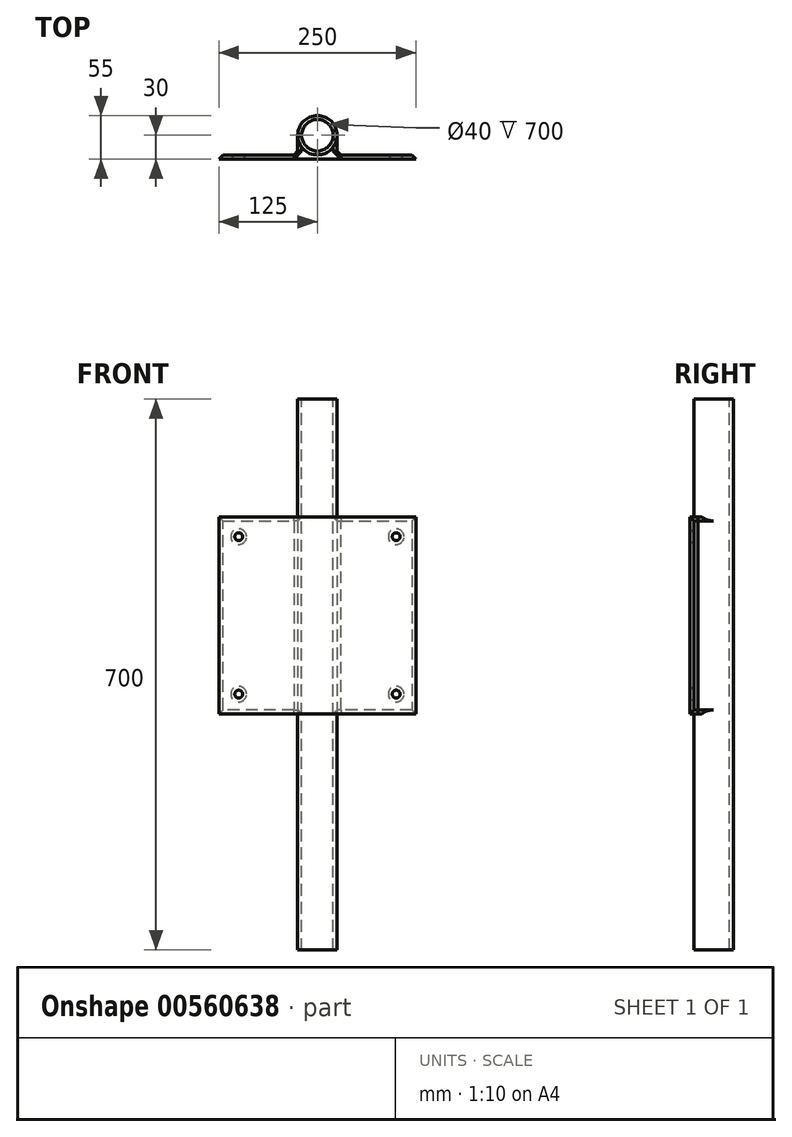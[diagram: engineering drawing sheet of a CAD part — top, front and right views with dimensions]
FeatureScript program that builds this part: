
annotation { "Feature Type Name" : "Feature", "Feature Type Description" : "" }
export const myFeature = defineFeature(function(context is Context, id is Id, definition is map)
    precondition{}
    {
        {
            var Q0;
            Q0=qCreatedBy(makeId("Top.planeOp"),FACE);
            var sketch = newSketch(context, id + "F0", { "sketchPlane" : qUnion([Q0])});
            skCircle(sketch, "E0", {"center": v(0, 0) * mm, "radius": 25 * mm});
            skLineSegment(sketch, "E1.bottom", {"start": v(-125, -25) * mm, "end": v(125, -25) * mm});
            skLineSegment(sketch, "E1.top", {"start": v(-125, -30) * mm, "end": v(125, -30) * mm});
            skLineSegment(sketch, "E1.left", {"start": v(-125, -25) * mm, "end": v(-125, -30) * mm});
            skLineSegment(sketch, "E1.right", {"start": v(125, -25) * mm, "end": v(125, -30) * mm});
            skLineSegment(sketch, "E2", {"start": v(25, 0) * mm, "end": v(25, -25) * mm});
            skLineSegment(sketch, "E3", {"start": v(-25, 0) * mm, "end": v(-25, -25) * mm});
            skSolve(sketch);
        }
        {
            var Q0;
            Q0 = qSketchRegion(id + "F0", true);
            var Q1;
            {var subQ0=sQuery(id+"F0.wireOp",EDGE,"E1.bottom");var subQ1=sQuery(id+"F0.wireOp",EDGE,"E0");var subQ2=makeQuery(id+"F0.imprint","INTERSECT",VERTEX,{"disambiguationData":[OD(0.0)],"derivedFrom":[subQ1,subQ0]});Q1=makeQuery(id+"F0.imprint","IMPRINT",FACE,{"disambiguationData":[TD([[makeQuery(id+"F0.imprint","IMPRINT",EDGE,{"disambiguationData":[TD([[subQ2,-1.0]])],"derivedFrom":subQ1}),1.0]])]});}
            extrude(context, id + "F1", {"entities" : qUnion([Q0, Q1]), "depth" : 250 * mm, "offsetDistance" : 25 * mm});
        }
        {
            var Q0;
            Q0=makeQuery(id+"F1.opExtrude","SWEPT_FACE",FACE,{"disambiguationData":[OSD([sQuery(id+"F0.wireOp",EDGE,"E1.top")])]});
            var sketch = newSketch(context, id + "F2", { "sketchPlane" : qUnion([Q0])});
            skLineSegment(sketch, "E4.bottom", {"start": v(-100, 225) * mm, "end": v(100, 225) * mm});
            skLineSegment(sketch, "E4.top", {"start": v(-100, 25) * mm, "end": v(100, 25) * mm});
            skLineSegment(sketch, "E4.left", {"start": v(-100, 225) * mm, "end": v(-100, 25) * mm});
            skLineSegment(sketch, "E4.right", {"start": v(100, 225) * mm, "end": v(100, 25) * mm});
            skCircle(sketch, "E5", {"center": v(-100, 225) * mm, "radius": 5 * mm});
            skCircle(sketch, "E6", {"center": v(100, 225) * mm, "radius": 5 * mm});
            skCircle(sketch, "E7", {"center": v(100, 25) * mm, "radius": 5 * mm});
            skCircle(sketch, "E8", {"center": v(-100, 25) * mm, "radius": 5 * mm});
            skSolve(sketch);
        }
        {
            var Q0;
            {var subQ0=sQuery(id+"F2.wireOp",EDGE,"E4.left");var subQ1=sQuery(id+"F2.wireOp",EDGE,"E4.bottom");var subQ2=makeQuery(id+"F2.imprint","INTERSECT",VERTEX,{"derivedFrom":[subQ1,subQ0]});Q0=makeQuery(id+"F2.imprint","IMPRINT",FACE,{"disambiguationData":[TD([[makeQuery(id+"F2.imprint","IMPRINT",EDGE,{"disambiguationData":[TD([[subQ2,-1.0]])],"derivedFrom":subQ1}),1.0]])]});}
            var Q1;
            {var subQ0=sQuery(id+"F2.wireOp",EDGE,"E4.left");var subQ1=sQuery(id+"F2.wireOp",EDGE,"E4.bottom");var subQ2=makeQuery(id+"F2.imprint","INTERSECT",VERTEX,{"derivedFrom":[subQ1,subQ0]});Q1=makeQuery(id+"F2.imprint","IMPRINT",FACE,{"disambiguationData":[TD([[makeQuery(id+"F2.imprint","IMPRINT",EDGE,{"disambiguationData":[TD([[subQ2,-1.0]])],"derivedFrom":subQ1}),-1.0]])]});}
            var Q2;
            {var subQ0=sQuery(id+"F2.wireOp",EDGE,"E4.right");var subQ1=sQuery(id+"F2.wireOp",EDGE,"E4.bottom");var subQ2=makeQuery(id+"F2.imprint","INTERSECT",VERTEX,{"derivedFrom":[subQ1,subQ0]});Q2=makeQuery(id+"F2.imprint","IMPRINT",FACE,{"disambiguationData":[TD([[makeQuery(id+"F2.imprint","IMPRINT",EDGE,{"disambiguationData":[TD([[subQ2,1.0]])],"derivedFrom":subQ1}),-1.0]])]});}
            var Q3;
            {var subQ0=sQuery(id+"F2.wireOp",EDGE,"E4.right");var subQ1=sQuery(id+"F2.wireOp",EDGE,"E4.bottom");var subQ2=makeQuery(id+"F2.imprint","INTERSECT",VERTEX,{"derivedFrom":[subQ1,subQ0]});Q3=makeQuery(id+"F2.imprint","IMPRINT",FACE,{"disambiguationData":[TD([[makeQuery(id+"F2.imprint","IMPRINT",EDGE,{"disambiguationData":[TD([[subQ2,1.0]])],"derivedFrom":subQ1}),1.0]])]});}
            var Q4;
            {var subQ0=sQuery(id+"F2.wireOp",EDGE,"E4.left");var subQ1=sQuery(id+"F2.wireOp",EDGE,"E4.top");var subQ2=makeQuery(id+"F2.imprint","INTERSECT",VERTEX,{"derivedFrom":[subQ1,subQ0]});Q4=makeQuery(id+"F2.imprint","IMPRINT",FACE,{"disambiguationData":[TD([[makeQuery(id+"F2.imprint","IMPRINT",EDGE,{"disambiguationData":[TD([[subQ2,-1.0]])],"derivedFrom":subQ1}),1.0]])]});}
            var Q5;
            {var subQ0=sQuery(id+"F2.wireOp",EDGE,"E4.left");var subQ1=sQuery(id+"F2.wireOp",EDGE,"E4.top");var subQ2=makeQuery(id+"F2.imprint","INTERSECT",VERTEX,{"derivedFrom":[subQ1,subQ0]});Q5=makeQuery(id+"F2.imprint","IMPRINT",FACE,{"disambiguationData":[TD([[makeQuery(id+"F2.imprint","IMPRINT",EDGE,{"disambiguationData":[TD([[subQ2,-1.0]])],"derivedFrom":subQ1}),-1.0]])]});}
            var Q6;
            {var subQ0=sQuery(id+"F2.wireOp",EDGE,"E4.right");var subQ1=sQuery(id+"F2.wireOp",EDGE,"E4.top");var subQ2=makeQuery(id+"F2.imprint","INTERSECT",VERTEX,{"derivedFrom":[subQ1,subQ0]});Q6=makeQuery(id+"F2.imprint","IMPRINT",FACE,{"disambiguationData":[TD([[makeQuery(id+"F2.imprint","IMPRINT",EDGE,{"disambiguationData":[TD([[subQ2,1.0]])],"derivedFrom":subQ1}),1.0]])]});}
            var Q7;
            {var subQ0=sQuery(id+"F2.wireOp",EDGE,"E4.right");var subQ1=sQuery(id+"F2.wireOp",EDGE,"E4.top");var subQ2=makeQuery(id+"F2.imprint","INTERSECT",VERTEX,{"derivedFrom":[subQ1,subQ0]});Q7=makeQuery(id+"F2.imprint","IMPRINT",FACE,{"disambiguationData":[TD([[makeQuery(id+"F2.imprint","IMPRINT",EDGE,{"disambiguationData":[TD([[subQ2,1.0]])],"derivedFrom":subQ1}),-1.0]])]});}
            extrude(context, id + "F3", {"entities" : qUnion([Q0, Q1, Q2, Q3, Q4, Q5, Q6, Q7]), "operationType" : NewBodyOperationType.REMOVE, "oppositeDirection" : true, "depth" : 25 * mm, "offsetDistance" : 25 * mm});
        }
        {
            var Q0;
            Q0=makeQuery(id+"F1.opExtrude","CAP_FACE",FACE,{"disambiguationData":[OSD([sQuery(id+"F0.wireOp",EDGE,"E0"),sQuery(id+"F0.wireOp",EDGE,"E1.bottom"),sQuery(id+"F0.wireOp",EDGE,"E1.top"),sQuery(id+"F0.wireOp",EDGE,"E1.left"),sQuery(id+"F0.wireOp",EDGE,"E1.right"),sQuery(id+"F0.wireOp",EDGE,"E2"),sQuery(id+"F0.wireOp",EDGE,"E3")])],"isStart":false});
            var sketch = newSketch(context, id + "F4", { "sketchPlane" : qUnion([Q0])});
            skCircle(sketch, "E9", {"center": v(0, 0) * mm, "radius": 25 * mm});
            skSolve(sketch);
        }
        {
            var Q0;
            Q0 = qSketchRegion(id + "F4", true);
            extrude(context, id + "F5", {"entities" : qUnion([Q0]), "operationType" : NewBodyOperationType.ADD, "depth" : 150 * mm, "offsetDistance" : 25 * mm});
        }
        {
            var Q0;
            Q0=makeQuery(id+"F1.opExtrude","CAP_FACE",FACE,{"disambiguationData":[OSD([sQuery(id+"F0.wireOp",EDGE,"E0"),sQuery(id+"F0.wireOp",EDGE,"E1.bottom"),sQuery(id+"F0.wireOp",EDGE,"E1.top"),sQuery(id+"F0.wireOp",EDGE,"E1.left"),sQuery(id+"F0.wireOp",EDGE,"E1.right"),sQuery(id+"F0.wireOp",EDGE,"E2"),sQuery(id+"F0.wireOp",EDGE,"E3")])],"isStart":true});
            var sketch = newSketch(context, id + "F6", { "sketchPlane" : qUnion([Q0])});
            skCircle(sketch, "E10", {"center": v(0, 0) * mm, "radius": 25 * mm});
            skSolve(sketch);
        }
        {
            var Q0;
            Q0 = qSketchRegion(id + "F6", true);
            extrude(context, id + "F7", {"entities" : qUnion([Q0]), "operationType" : NewBodyOperationType.ADD, "depth" : 300 * mm, "offsetDistance" : 25 * mm});
        }
        {
            var Q0;
            Q0=makeQuery(id+"F5.opExtrude","CAP_FACE",FACE,{"disambiguationData":[OSD([sQuery(id+"F4.wireOp",EDGE,"E9")])],"isStart":false});
            var sketch = newSketch(context, id + "F8", { "sketchPlane" : qUnion([Q0])});
            skCircle(sketch, "E11", {"center": v(0, 0) * mm, "radius": 20 * mm});
            skSolve(sketch);
        }
        {
            var Q0;
            Q0 = qSketchRegion(id + "F8", true);
            extrude(context, id + "F9", {"entities" : qUnion([Q0]), "operationType" : NewBodyOperationType.REMOVE, "endBound" : BoundingType.THROUGH_ALL, "oppositeDirection" : true, "depth" : 25 * mm, "offsetDistance" : 25 * mm});
        }
        {
            var Q0;
            {var subQ0=sQuery(id+"F0.wireOp",EDGE,"E1.bottom");Q0=makeQuery(id+"F1.opExtrude","SWEPT_FACE",FACE,{"disambiguationData":[OSD([subQ0]),TDD([makeQuery(id+"F0.imprint","IMPRINT",EDGE,{"disambiguationData":[TD([[makeQuery(id+"F0.imprint","INTERSECT",VERTEX,{"derivedFrom":[subQ0,sQuery(id+"F0.wireOp",EDGE,"E1.right")]}),1.0]])],"derivedFrom":subQ0})])]});}
            var Q1;
            {var subQ0=sQuery(id+"F0.wireOp",EDGE,"E1.bottom");Q1=makeQuery(id+"F1.opExtrude","SWEPT_FACE",FACE,{"disambiguationData":[OSD([subQ0]),TDD([makeQuery(id+"F0.imprint","IMPRINT",EDGE,{"disambiguationData":[TD([[makeQuery(id+"F0.imprint","INTERSECT",VERTEX,{"derivedFrom":[subQ0,sQuery(id+"F0.wireOp",EDGE,"E1.left")]}),-1.0]])],"derivedFrom":subQ0})])]});}
            chamfer(context, id + "F10", {"entities" : qUnion([Q0, Q1]), "width" : 5 * mm, "tangentPropagation" : true});
        }
    });
